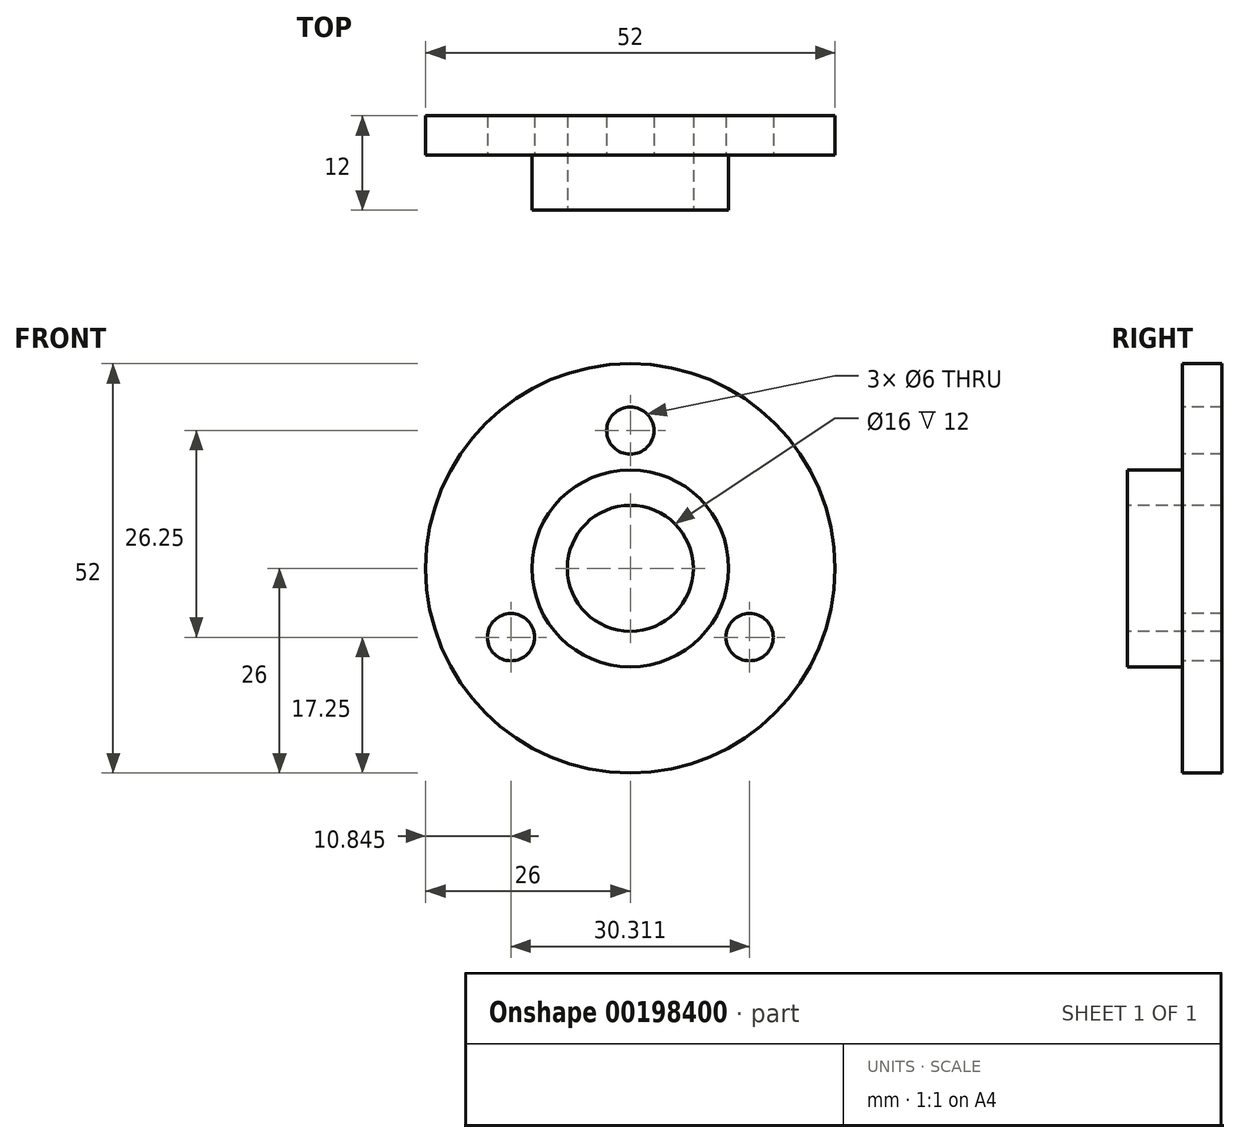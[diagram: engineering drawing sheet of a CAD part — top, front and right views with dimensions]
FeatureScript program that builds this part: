
annotation { "Feature Type Name" : "Feature", "Feature Type Description" : "" }
export const myFeature = defineFeature(function(context is Context, id is Id, definition is map)
    precondition{}
    {
        {
            var Q0;
            Q0=qCreatedBy(makeId("Front.planeOp"),FACE);
            var sketch = newSketch(context, id + "F0", { "sketchPlane" : qUnion([Q0])});
            skCircle(sketch, "E0", {"center": v(0, 0) * mm, "radius": 26 * mm});
            skSolve(sketch);
        }
        {
            var Q0;
            Q0 = qSketchRegion(id + "F0", true);
            extrude(context, id + "F1", {"entities" : qUnion([Q0]), "depth" : 5 * mm});
        }
        {
            var Q0;
            Q0=makeQuery(id+"F1.opExtrude","CAP_FACE",FACE,{"disambiguationData":[OSD([sQuery(id+"F0.wireOp",EDGE,"E0")])],"isStart":false});
            var sketch = newSketch(context, id + "F2", { "sketchPlane" : qUnion([Q0])});
            skCircle(sketch, "E1", {"center": v(0, 0) * mm, "radius": 12.5 * mm});
            skSolve(sketch);
        }
        {
            var Q0;
            Q0 = qSketchRegion(id + "F2", true);
            extrude(context, id + "F3", {"entities" : qUnion([Q0]), "operationType" : NewBodyOperationType.ADD, "depth" : 7 * mm});
        }
        {
            var Q0;
            Q0=makeQuery(id+"F1.opExtrude","CAP_FACE",FACE,{"disambiguationData":[OSD([sQuery(id+"F0.wireOp",EDGE,"E0")])],"isStart":false});
            var sketch = newSketch(context, id + "F4", { "sketchPlane" : qUnion([Q0])});
            skCircle(sketch, "E2", {"center": v(0, 17.5) * mm, "radius": 3 * mm});
            skCircle(sketch, "E3.1.0", {"center": v(-15.16, -8.75) * mm, "radius": 3 * mm});
            skCircle(sketch, "E3.2.0", {"center": v(15.16, -8.75) * mm, "radius": 3 * mm});
            skPoint(sketch, "E3.center", {"position": v(0, 0) * mm});
            skSolve(sketch);
        }
        {
            var Q0;
            Q0 = qSketchRegion(id + "F4", true);
            extrude(context, id + "F5", {"entities" : qUnion([Q0]), "operationType" : NewBodyOperationType.REMOVE, "oppositeDirection" : true, "depth" : 25 * mm});
        }
        {
            var Q0;
            Q0=makeQuery(id+"F3.opExtrude","CAP_FACE",FACE,{"disambiguationData":[OSD([sQuery(id+"F2.wireOp",EDGE,"E1")])],"isStart":false});
            var sketch = newSketch(context, id + "F6", { "sketchPlane" : qUnion([Q0])});
            skCircle(sketch, "E4", {"center": v(0, 0) * mm, "radius": 8 * mm});
            skSolve(sketch);
        }
        {
            var Q0;
            Q0 = qSketchRegion(id + "F6", true);
            extrude(context, id + "F7", {"entities" : qUnion([Q0]), "operationType" : NewBodyOperationType.REMOVE, "oppositeDirection" : true, "depth" : 25 * mm});
        }
    });
